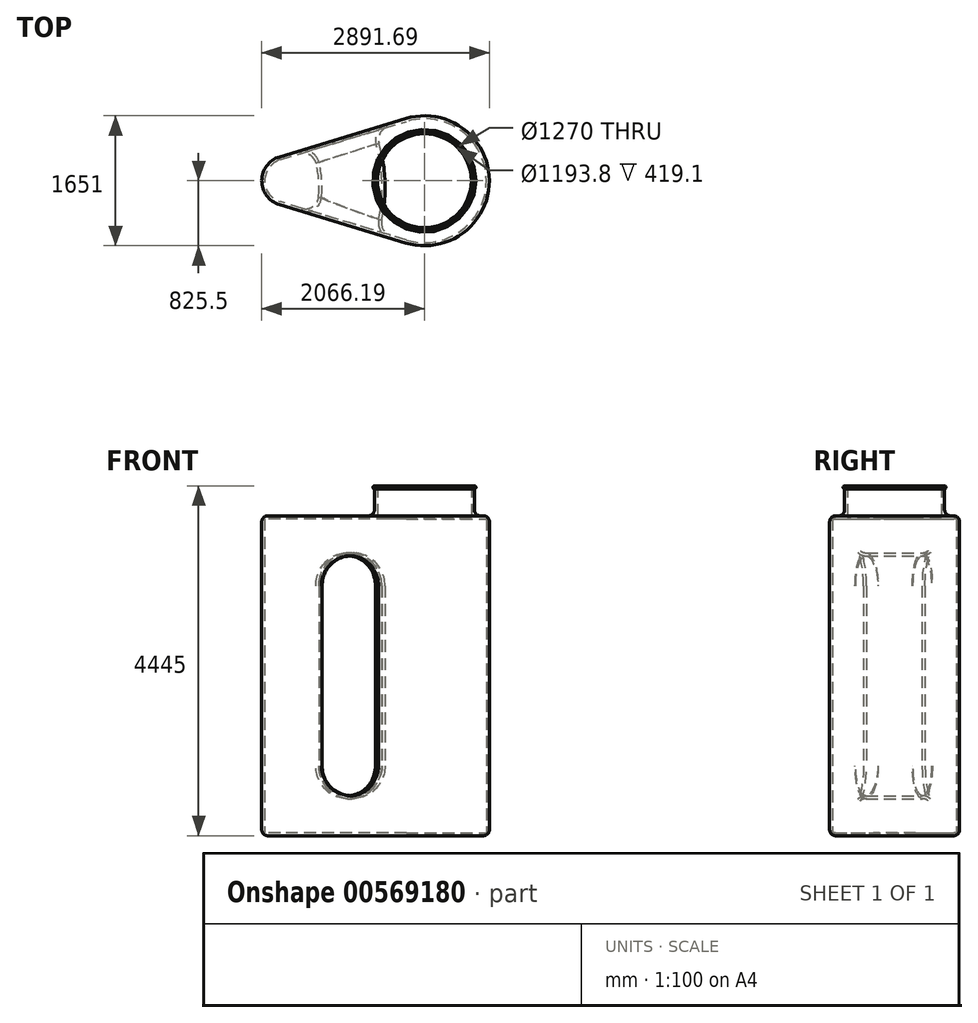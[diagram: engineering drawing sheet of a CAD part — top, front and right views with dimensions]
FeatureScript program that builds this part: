
annotation { "Feature Type Name" : "Feature", "Feature Type Description" : "" }
export const myFeature = defineFeature(function(context is Context, id is Id, definition is map)
    precondition{}
    {
        {
            var Q0;
            Q0=qCreatedBy(makeId("Top.planeOp"),FACE);
            var sketch = newSketch(context, id + "F0", { "sketchPlane" : qUnion([Q0])});
            skArc(sketch, "E0", {"start": v(-239.81, -789.9) * mm, "mid": v(825.5, 0) * mm, "end": v(-239.81, 789.9) * mm});
            skLineSegment(sketch, "E1", {"start": v(-1748.7, 331.8) * mm, "end": v(-239.81, 789.9) * mm});
            skPoint(sketch, "E2.orphan", {"position": v(2.26, 863.4) * mm});
            skPoint(sketch, "E3.orphan", {"position": v(0.22, -870.36) * mm});
            skArc(sketch, "E4", {"start": v(-1840.93, 303.8) * mm, "mid": v(-2066.2, 0) * mm, "end": v(-1840.93, -303.8) * mm});
            skLineSegment(sketch, "E5", {"start": v(-239.81, -789.9) * mm, "end": v(-1840.93, -303.8) * mm});
            skLineSegment(sketch, "E6", {"start": v(-1840.93, 303.8) * mm, "end": v(-1748.7, 331.8) * mm});
            skSolve(sketch);
        }
        {
            var Q0;
            Q0=makeQuery(id+"F0.imprint","IMPRINT",FACE,{"disambiguationData":[TD([[makeQuery(id+"F0.imprint","IMPRINT",EDGE,{"derivedFrom":sQuery(id+"F0.wireOp",EDGE,"E0")}),1.0]])]});
            extrude(context, id + "F1", {"entities" : qUnion([Q0]), "depth" : 4064 * mm, "offsetDistance" : 25.4 * mm});
        }
        {
            var Q0;
            Q0=makeQuery(id+"F1.opExtrude","SWEPT_FACE",FACE,{"disambiguationData":[OSD([sQuery(id+"F0.wireOp",EDGE,"E5")])]});
            var sketch = newSketch(context, id + "F2", { "sketchPlane" : qUnion([Q0])});
            skArc(sketch, "E7", {"start": v(-403.28, 3175) * mm, "mid": v(-784.28, 3556) * mm, "end": v(-1165.28, 3175) * mm});
            skArc(sketch, "E8", {"start": v(-1165.28, 889) * mm, "mid": v(-784.28, 508) * mm, "end": v(-403.28, 889) * mm});
            skLineSegment(sketch, "E9", {"start": v(-403.28, 3175) * mm, "end": v(-403.28, 889) * mm});
            skLineSegment(sketch, "E10", {"start": v(-1165.28, 3175) * mm, "end": v(-1165.28, 889) * mm});
            skLineSegment(sketch, "E11", {"start": v(-2435.28, 5362.98) * mm, "end": v(-2435.28, -1954.74) * mm, "construction": true});
            skSolve(sketch);
        }
        {
            var Q0;
            Q0 = qSketchRegion(id + "F2", true);
            var Q1;
            Q1=sQuery(id+"F2.wireOp",EDGE,"E11");
            revolve(context, id + "F3", {"operationType" : NewBodyOperationType.REMOVE, "entities" : qUnion([Q0]), "axis" : qUnion([Q1]), "revolveType" : RevolveType.FULL, "oppositeDirection" : true});
        }
        {
            var Q0;
            Q0=makeQuery(id+"F1.opExtrude","CAP_FACE",FACE,{"disambiguationData":[OSD([sQuery(id+"F0.wireOp",EDGE,"E0"),sQuery(id+"F0.wireOp",EDGE,"E4"),sQuery(id+"F0.wireOp",EDGE,"E1"),sQuery(id+"F0.wireOp",EDGE,"E5"),sQuery(id+"F0.wireOp",EDGE,"E6")])],"isStart":false});
            var sketch = newSketch(context, id + "F4", { "sketchPlane" : qUnion([Q0])});
            skCircle(sketch, "E12", {"center": v(0, 0) * mm, "radius": 635 * mm});
            skSolve(sketch);
        }
        {
            var Q0;
            Q0 = qSketchRegion(id + "F4", true);
            extrude(context, id + "F5", {"entities" : qUnion([Q0]), "operationType" : NewBodyOperationType.ADD, "depth" : 381 * mm, "offsetDistance" : 25.4 * mm});
        }
        {
            var Q0;
            Q0=qCreatedBy(makeId("Front.planeOp"),FACE);
            var sketch = newSketch(context, id + "F6", { "sketchPlane" : qUnion([Q0])});
            skLineSegment(sketch, "E13", {"start": v(635, 4650) * mm, "end": v(635, 4201.9) * mm, "construction": true});
            skLineSegment(sketch, "E14", {"start": v(0, 4787.56) * mm, "end": v(0, 3062.06) * mm, "construction": true});
            skArc(sketch, "E15", {"start": v(635, 4406.9) * mm, "mid": v(654.05, 4425.95) * mm, "end": v(635, 4445) * mm});
            skLineSegment(sketch, "E16", {"start": v(635, 4445) * mm, "end": v(635, 4406.9) * mm});
            skSolve(sketch);
        }
        {
            var Q0;
            Q0=makeQuery(id+"F6.imprint","IMPRINT",FACE,{"disambiguationData":[TD([[makeQuery(id+"F6.imprint","IMPRINT",EDGE,{"derivedFrom":sQuery(id+"F6.wireOp",EDGE,"E15")}),1.0]])]});
            var Q1;
            Q1=sQuery(id+"F6.wireOp",EDGE,"E14");
            revolve(context, id + "F7", {"entities" : qUnion([Q0]), "axis" : qUnion([Q1]), "revolveType" : RevolveType.FULL});
        }
        {
            var Q0;
            Q0=makeQuery(id+"F3.boolean.opBoolean","INTERSECT",EDGE,{"derivedFrom":[makeQuery(id+"F1.opExtrude","SWEPT_FACE",FACE,{"disambiguationData":[OSD([sQuery(id+"F0.wireOp",EDGE,"E5")])]}),makeQuery(id+"F3.opRevolve","SWEPT_FACE",FACE,{"disambiguationData":[OSD([sQuery(id+"F2.wireOp",EDGE,"E10")])]})]});
            var Q1;
            Q1=makeQuery(id+"F3.boolean.opBoolean","INTERSECT",EDGE,{"derivedFrom":[makeQuery(id+"F1.opExtrude","SWEPT_FACE",FACE,{"disambiguationData":[OSD([sQuery(id+"F0.wireOp",EDGE,"E1"),sQuery(id+"F0.wireOp",EDGE,"E6")])]}),makeQuery(id+"F3.opRevolve","SWEPT_FACE",FACE,{"disambiguationData":[OSD([sQuery(id+"F2.wireOp",EDGE,"E10")])]})]});
            fillet(context, id + "F8", {"entities" : qUnion([Q0, Q1]), "radius" : 203.2 * mm, "tangentPropagation" : true, "allowEdgeOverflow" : false});
        }
        {
            var Q0;
            Q0=makeQuery(id+"F5.opExtrude","CAP_FACE",FACE,{"disambiguationData":[OSD([sQuery(id+"F4.wireOp",EDGE,"E12")])],"isStart":false});
            shell(context, id + "F9", {"entities" : qUnion([Q0]), "thickness" : 38.1 * mm});
        }
        {
            var Q0;
            Q0=makeQuery(id+"F1.opExtrude","CAP_EDGE",EDGE,{"disambiguationData":[OSD([sQuery(id+"F0.wireOp",EDGE,"E1"),sQuery(id+"F0.wireOp",EDGE,"E6")])],"isStart":false});
            var Q1;
            Q1=makeQuery(id+"F1.opExtrude","CAP_EDGE",EDGE,{"disambiguationData":[OSD([sQuery(id+"F0.wireOp",EDGE,"E4")])],"isStart":false});
            var Q2;
            Q2=makeQuery(id+"F1.opExtrude","CAP_EDGE",EDGE,{"disambiguationData":[OSD([sQuery(id+"F0.wireOp",EDGE,"E0")])],"isStart":false});
            var Q3;
            Q3=makeQuery(id+"F1.opExtrude","CAP_EDGE",EDGE,{"disambiguationData":[OSD([sQuery(id+"F0.wireOp",EDGE,"E5")])],"isStart":false});
            var Q4;
            Q4=makeQuery(id+"F1.opExtrude","CAP_EDGE",EDGE,{"disambiguationData":[OSD([sQuery(id+"F0.wireOp",EDGE,"E5")])],"isStart":true});
            var Q5;
            Q5=makeQuery(id+"F1.opExtrude","CAP_EDGE",EDGE,{"disambiguationData":[OSD([sQuery(id+"F0.wireOp",EDGE,"E0")])],"isStart":true});
            var Q6;
            Q6=makeQuery(id+"F1.opExtrude","CAP_EDGE",EDGE,{"disambiguationData":[OSD([sQuery(id+"F0.wireOp",EDGE,"E1"),sQuery(id+"F0.wireOp",EDGE,"E6")])],"isStart":true});
            var Q7;
            Q7=makeQuery(id+"F1.opExtrude","CAP_EDGE",EDGE,{"disambiguationData":[OSD([sQuery(id+"F0.wireOp",EDGE,"E4")])],"isStart":true});
            fillet(context, id + "F10", {"entities" : qUnion([Q0, Q1, Q2, Q3, Q4, Q5, Q6, Q7]), "radius" : 76.2 * mm, "tangentPropagation" : true, "allowEdgeOverflow" : false});
        }
        {
            var Q0;
            Q0=makeQuery(id+"F1.opExtrude","CAP_FACE",FACE,{"disambiguationData":[OSD([sQuery(id+"F0.wireOp",EDGE,"E0"),sQuery(id+"F0.wireOp",EDGE,"E4"),sQuery(id+"F0.wireOp",EDGE,"E1"),sQuery(id+"F0.wireOp",EDGE,"E5"),sQuery(id+"F0.wireOp",EDGE,"E6")])],"isStart":false});
            fillet(context, id + "F11", {"entities" : qUnion([Q0]), "radius" : 76.2 * mm, "tangentPropagation" : true, "allowEdgeOverflow" : false});
        }
    });
